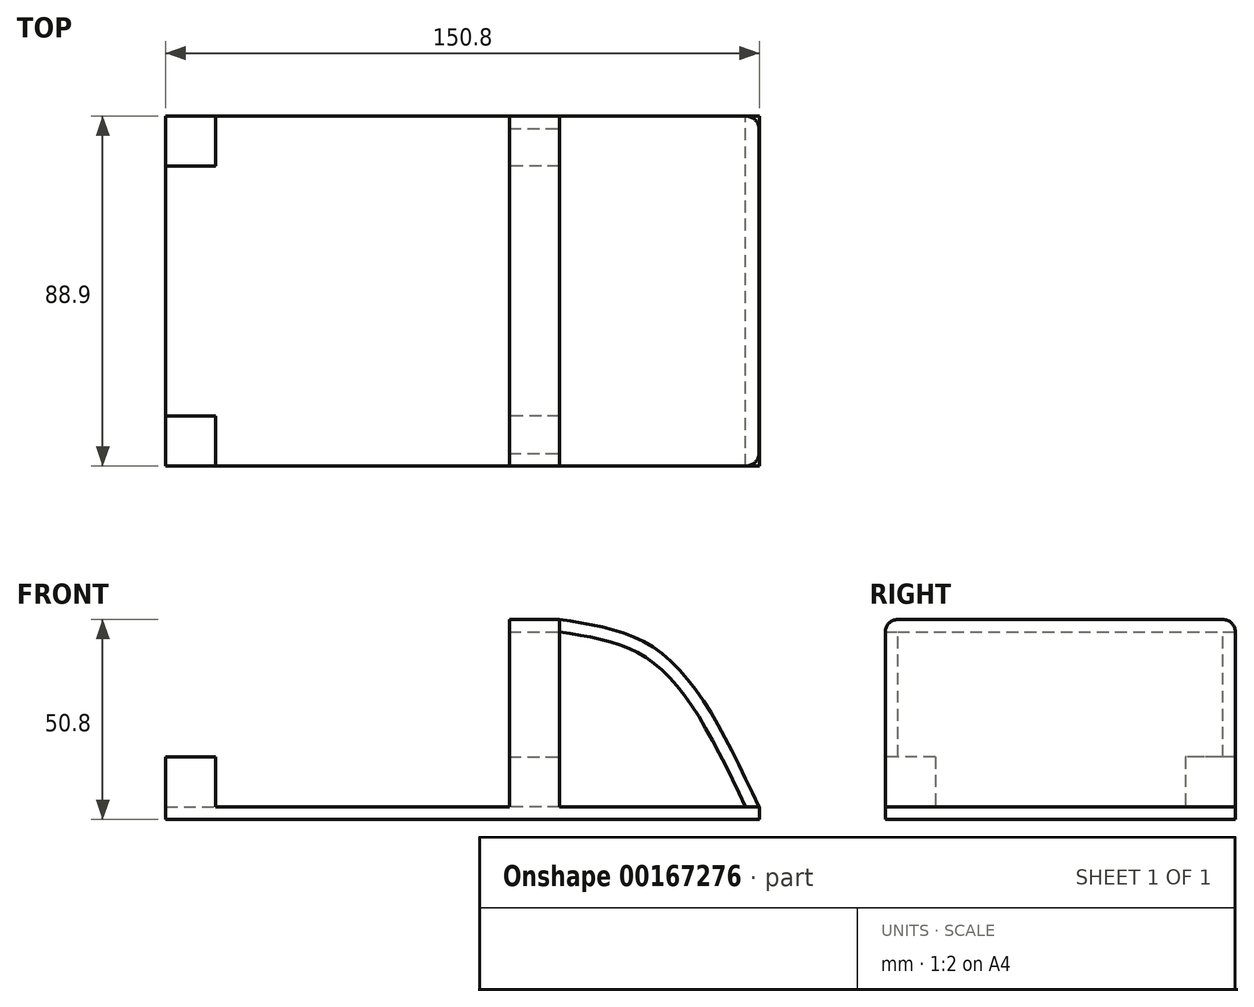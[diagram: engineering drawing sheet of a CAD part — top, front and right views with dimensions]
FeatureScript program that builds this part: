
annotation { "Feature Type Name" : "Feature", "Feature Type Description" : "" }
export const myFeature = defineFeature(function(context is Context, id is Id, definition is map)
    precondition{}
    {
        {
            var Q0;
            Q0=qCreatedBy(makeId("Top.planeOp"),FACE);
            var sketch = newSketch(context, id + "F0", { "sketchPlane" : qUnion([Q0])});
            skLineSegment(sketch, "E0.bottom", {"start": v(50, 44.45) * mm, "end": v(-50, 44.45) * mm});
            skLineSegment(sketch, "E0.top", {"start": v(50, -44.45) * mm, "end": v(-50, -44.45) * mm});
            skLineSegment(sketch, "E0.left", {"start": v(50, 44.45) * mm, "end": v(50, -44.45) * mm});
            skLineSegment(sketch, "E0.right", {"start": v(-50, 44.45) * mm, "end": v(-50, -44.45) * mm});
            skPoint(sketch, "E0.middle", {"position": v(0, 0) * mm});
            skSolve(sketch);
        }
        {
            var Q0;
            Q0=makeQuery(id+"F0.imprint","IMPRINT",FACE,{"disambiguationData":[TD([[makeQuery(id+"F0.imprint","IMPRINT",EDGE,{"derivedFrom":sQuery(id+"F0.wireOp",EDGE,"E0.bottom")}),1.0]])]});
            extrude(context, id + "F1", {"entities" : qUnion([Q0]), "depth" : 3.17 * mm});
        }
        {
            var Q0;
            Q0=makeQuery(id+"F1.opExtrude","CAP_FACE",FACE,{"disambiguationData":[OSD([sQuery(id+"F0.wireOp",EDGE,"E0.bottom"),sQuery(id+"F0.wireOp",EDGE,"E0.top"),sQuery(id+"F0.wireOp",EDGE,"E0.left"),sQuery(id+"F0.wireOp",EDGE,"E0.right")])],"isStart":false});
            var sketch = newSketch(context, id + "F2", { "sketchPlane" : qUnion([Q0])});
            skLineSegment(sketch, "E1.bottom", {"start": v(-50, 44.45) * mm, "end": v(-37.3, 44.45) * mm});
            skLineSegment(sketch, "E1.top", {"start": v(-50, 31.75) * mm, "end": v(-37.3, 31.75) * mm});
            skLineSegment(sketch, "E1.left", {"start": v(-50, 44.45) * mm, "end": v(-50, 31.75) * mm});
            skLineSegment(sketch, "E1.right", {"start": v(-37.3, 44.45) * mm, "end": v(-37.3, 31.75) * mm});
            skLineSegment(sketch, "E2.MirrorCS", {"start": v(50, 44.45) * mm, "end": v(37.3, 44.45) * mm});
            skLineSegment(sketch, "E3.MirrorCS", {"start": v(50, 44.45) * mm, "end": v(50, 31.75) * mm});
            skLineSegment(sketch, "E4.MirrorCS", {"start": v(37.3, 44.45) * mm, "end": v(37.3, 31.75) * mm});
            skLineSegment(sketch, "E5.MirrorCS", {"start": v(50, 31.75) * mm, "end": v(37.3, 31.75) * mm});
            skLineSegment(sketch, "E6.MirrorCS", {"start": v(-50, -44.45) * mm, "end": v(-37.3, -44.45) * mm});
            skLineSegment(sketch, "E7.MirrorCS", {"start": v(-37.3, -44.45) * mm, "end": v(-37.3, -31.75) * mm});
            skLineSegment(sketch, "E8.MirrorCS", {"start": v(-50, -31.75) * mm, "end": v(-37.3, -31.75) * mm});
            skLineSegment(sketch, "E9.MirrorCS", {"start": v(-50, -44.45) * mm, "end": v(-50, -31.75) * mm});
            skLineSegment(sketch, "E10.MirrorCS", {"start": v(50, -44.45) * mm, "end": v(37.3, -44.45) * mm});
            skLineSegment(sketch, "E11.MirrorCS", {"start": v(37.3, -44.45) * mm, "end": v(37.3, -31.75) * mm});
            skLineSegment(sketch, "E12.MirrorCS", {"start": v(50, -44.45) * mm, "end": v(50, -31.75) * mm});
            skLineSegment(sketch, "E13.MirrorCS", {"start": v(50, -31.75) * mm, "end": v(37.3, -31.75) * mm});
            skSolve(sketch);
        }
        {
            var Q0;
            Q0 = qSketchRegion(id + "F2", true);
            extrude(context, id + "F3", {"entities" : qUnion([Q0]), "operationType" : NewBodyOperationType.ADD, "depth" : 12.7 * mm});
        }
        {
            var Q0;
            Q0=makeQuery(id+"F3.boolean.opBoolean","MERGE",FACE,{"derivedFrom":[makeQuery(id+"F1.opExtrude","SWEPT_FACE",FACE,{"disambiguationData":[OSD([sQuery(id+"F0.wireOp",EDGE,"E0.left")])]}),makeQuery(id+"F3.opExtrude","SWEPT_FACE",FACE,{"disambiguationData":[OSD([sQuery(id+"F2.wireOp",EDGE,"E3.MirrorCS")])]}),makeQuery(id+"F3.opExtrude","SWEPT_FACE",FACE,{"disambiguationData":[OSD([sQuery(id+"F2.wireOp",EDGE,"E12.MirrorCS")])]})]});
            var sketch = newSketch(context, id + "F4", { "sketchPlane" : qUnion([Q0])});
            skLineSegment(sketch, "E14.bottom", {"start": v(-44.45, 0) * mm, "end": v(44.45, 0) * mm});
            skLineSegment(sketch, "E14.top", {"start": v(-41.28, 50.8) * mm, "end": v(41.27, 50.8) * mm});
            skLineSegment(sketch, "E14.left", {"start": v(-44.45, 0) * mm, "end": v(-44.45, 47.63) * mm});
            skLineSegment(sketch, "E14.right", {"start": v(44.45, 0) * mm, "end": v(44.45, 47.63) * mm});
            skPoint(sketch, "E15.visualSharp", {"position": v(-44.45, 50.8) * mm});
            skArc(sketch, "E15.filletArc", {"start": v(-41.28, 50.8) * mm, "mid": v(-43.52, 49.87) * mm, "end": v(-44.45, 47.63) * mm});
            skPoint(sketch, "E16.visualSharp", {"position": v(44.45, 50.8) * mm});
            skArc(sketch, "E16.filletArc", {"start": v(44.45, 47.63) * mm, "mid": v(43.52, 49.87) * mm, "end": v(41.27, 50.8) * mm});
            skLineSegment(sketch, "E17.0", {"start": v(41.28, 0) * mm, "end": v(41.27, 47.63) * mm});
            skLineSegment(sketch, "E17.1", {"start": v(-41.28, 47.63) * mm, "end": v(41.27, 47.63) * mm});
            skLineSegment(sketch, "E17.2", {"start": v(-41.27, 0) * mm, "end": v(-41.28, 47.63) * mm});
            skSolve(sketch);
        }
        {
            var Q0;
            Q0=makeQuery(id+"F4.imprint","IMPRINT",FACE,{"disambiguationData":[TD([[makeQuery(id+"F4.imprint","IMPRINT",EDGE,{"derivedFrom":sQuery(id+"F4.wireOp",EDGE,"E14.top")}),-1.0]])]});
            extrude(context, id + "F5", {"entities" : qUnion([Q0]), "operationType" : NewBodyOperationType.ADD, "oppositeDirection" : true, "depth" : 12.7 * mm});
        }
        {
            var Q0;
            {var subQ0=sQuery(id+"F2.wireOp",EDGE,"E12.MirrorCS");var subQ1=sQuery(id+"F2.wireOp",EDGE,"E3.MirrorCS");Q0=makeQuery(id+"F5.boolean.opBoolean","MERGE",FACE,{"derivedFrom":[makeQuery(id+"F3.boolean.opBoolean","MERGE",FACE,{"derivedFrom":[makeQuery(id+"F1.opExtrude","SWEPT_FACE",FACE,{"disambiguationData":[OSD([sQuery(id+"F0.wireOp",EDGE,"E0.left")])]}),makeQuery(id+"F3.opExtrude","SWEPT_FACE",FACE,{"disambiguationData":[OSD([subQ1])]}),makeQuery(id+"F3.opExtrude","SWEPT_FACE",FACE,{"disambiguationData":[OSD([subQ0])]})]}),makeQuery(id+"F5.opExtrude","CAP_FACE",FACE,{"disambiguationData":[OSD([subQ1,subQ0,sQuery(id+"F4.wireOp",EDGE,"E14.top"),sQuery(id+"F4.wireOp",EDGE,"E14.left"),sQuery(id+"F4.wireOp",EDGE,"E14.right"),sQuery(id+"F4.wireOp",EDGE,"E15.filletArc"),sQuery(id+"F4.wireOp",EDGE,"E16.filletArc"),sQuery(id+"F4.wireOp",EDGE,"E17.0"),sQuery(id+"F4.wireOp",EDGE,"E17.1"),sQuery(id+"F4.wireOp",EDGE,"E17.2")])],"isStart":true})]});}
            var sketch = newSketch(context, id + "F6", { "sketchPlane" : qUnion([Q0])});
            skLineSegment(sketch, "E18.bottom", {"start": v(-44.45, 0) * mm, "end": v(44.45, 0) * mm});
            skLineSegment(sketch, "E18.top", {"start": v(-44.45, 3.18) * mm, "end": v(44.45, 3.18) * mm});
            skLineSegment(sketch, "E18.left", {"start": v(-44.45, 0) * mm, "end": v(-44.45, 3.18) * mm});
            skLineSegment(sketch, "E18.right", {"start": v(44.45, 0) * mm, "end": v(44.45, 3.18) * mm});
            skSolve(sketch);
        }
        {
            var Q0;
            Q0=makeQuery(id+"F6.imprint","IMPRINT",FACE,{"disambiguationData":[TD([[makeQuery(id+"F6.imprint","IMPRINT",EDGE,{"derivedFrom":sQuery(id+"F6.wireOp",EDGE,"E18.bottom")}),-1.0]])]});
            extrude(context, id + "F7", {"entities" : qUnion([Q0]), "operationType" : NewBodyOperationType.ADD, "depth" : 50.8 * mm});
        }
        {
            var Q0;
            {var subQ0=sQuery(id+"F2.wireOp",EDGE,"E12.MirrorCS");var subQ1=sQuery(id+"F2.wireOp",EDGE,"E3.MirrorCS");Q0=makeQuery(id+"F5.boolean.opBoolean","MERGE",FACE,{"derivedFrom":[makeQuery(id+"F3.boolean.opBoolean","MERGE",FACE,{"derivedFrom":[makeQuery(id+"F1.opExtrude","SWEPT_FACE",FACE,{"disambiguationData":[OSD([sQuery(id+"F0.wireOp",EDGE,"E0.left")])]}),makeQuery(id+"F3.opExtrude","SWEPT_FACE",FACE,{"disambiguationData":[OSD([subQ1])]}),makeQuery(id+"F3.opExtrude","SWEPT_FACE",FACE,{"disambiguationData":[OSD([subQ0])]})]}),makeQuery(id+"F5.opExtrude","CAP_FACE",FACE,{"disambiguationData":[OSD([subQ1,subQ0,sQuery(id+"F4.wireOp",EDGE,"E14.top"),sQuery(id+"F4.wireOp",EDGE,"E14.left"),sQuery(id+"F4.wireOp",EDGE,"E14.right"),sQuery(id+"F4.wireOp",EDGE,"E15.filletArc"),sQuery(id+"F4.wireOp",EDGE,"E16.filletArc"),sQuery(id+"F4.wireOp",EDGE,"E17.0"),sQuery(id+"F4.wireOp",EDGE,"E17.1"),sQuery(id+"F4.wireOp",EDGE,"E17.2")])],"isStart":true})]});}
            var sketch = newSketch(context, id + "F8", { "sketchPlane" : qUnion([Q0])});
            skLineSegment(sketch, "E19.bottom", {"start": v(-44.45, 47.63) * mm, "end": v(44.45, 47.63) * mm});
            skLineSegment(sketch, "E19.top", {"start": v(-44.45, 50.8) * mm, "end": v(44.45, 50.8) * mm});
            skLineSegment(sketch, "E19.left", {"start": v(-44.45, 47.63) * mm, "end": v(-44.45, 50.8) * mm});
            skLineSegment(sketch, "E19.right", {"start": v(44.45, 47.63) * mm, "end": v(44.45, 50.8) * mm});
            skSolve(sketch);
        }
        {
            var Q0;
            {var subQ0=sQuery(id+"F4.wireOp",EDGE,"E14.right");Q0=makeQuery(id+"F7.boolean.opBoolean","MERGE",FACE,{"derivedFrom":[makeQuery(id+"FF1Wfgs5Gt3Le0P_1.1.F5.boolean.opBoolean","MERGE",FACE,{"derivedFrom":[makeQuery(id+"F5.boolean.opBoolean","MERGE",FACE,{"derivedFrom":[makeQuery(id+"F3.boolean.opBoolean","MERGE",FACE,{"derivedFrom":[makeQuery(id+"F1.opExtrude","SWEPT_FACE",FACE,{"disambiguationData":[OSD([sQuery(id+"F0.wireOp",EDGE,"E0.bottom")])]}),makeQuery(id+"F3.opExtrude","SWEPT_FACE",FACE,{"disambiguationData":[OSD([sQuery(id+"F2.wireOp",EDGE,"E2.MirrorCS")])]}),makeQuery(id+"F3.opExtrude","SWEPT_FACE",FACE,{"disambiguationData":[OSD([sQuery(id+"F2.wireOp",EDGE,"E1.bottom")])]})]}),makeQuery(id+"F5.opExtrude","SWEPT_FACE",FACE,{"disambiguationData":[OSD([subQ0])]})]}),makeQuery(id+"FF1Wfgs5Gt3Le0P_1.1.F5.opExtrude","SWEPT_FACE",FACE,{"disambiguationData":[OSD([subQ0])]})]}),makeQuery(id+"F7.opExtrude","SWEPT_FACE",FACE,{"disambiguationData":[OSD([sQuery(id+"F6.wireOp",EDGE,"E18.right")])]})]});}
            var sketch = newSketch(context, id + "F9", { "sketchPlane" : qUnion([Q0])});
            skFitSpline(sketch, "E20", {"points": [v(-50, 50.88) * mm, v(-76.25, 42.09) * mm, v(-100.8, 3.18) * mm], "startDerivative": vector(-63.7, -9.42) * mm, "endDerivative": vector(-38.94, -82.9) * mm});
            skSolve(sketch);
        }
        {
            var Q0;
            {var subQ1=makeQuery(id+"F5.opExtrude","CAP_EDGE",EDGE,{"disambiguationData":[OSD([sQuery(id+"F4.wireOp",EDGE,"E15.filletArc")])],"isStart":true});Q0=makeQuery(id+"F8.imprint","IMPRINT",FACE,{"disambiguationData":[TD([[makeQuery(id+"F8.imprint","IMPRINT",EDGE,{"derivedFrom":subQ1}),1.0]])]});}
            var Q1;
            Q1=sQuery(id+"F9.wireOp",EDGE,"E20");
            sweep(context, id + "F10", {"operationType" : NewBodyOperationType.ADD, "profiles" : qUnion([Q0]), "path" : qUnion([Q1])});
        }
    });
